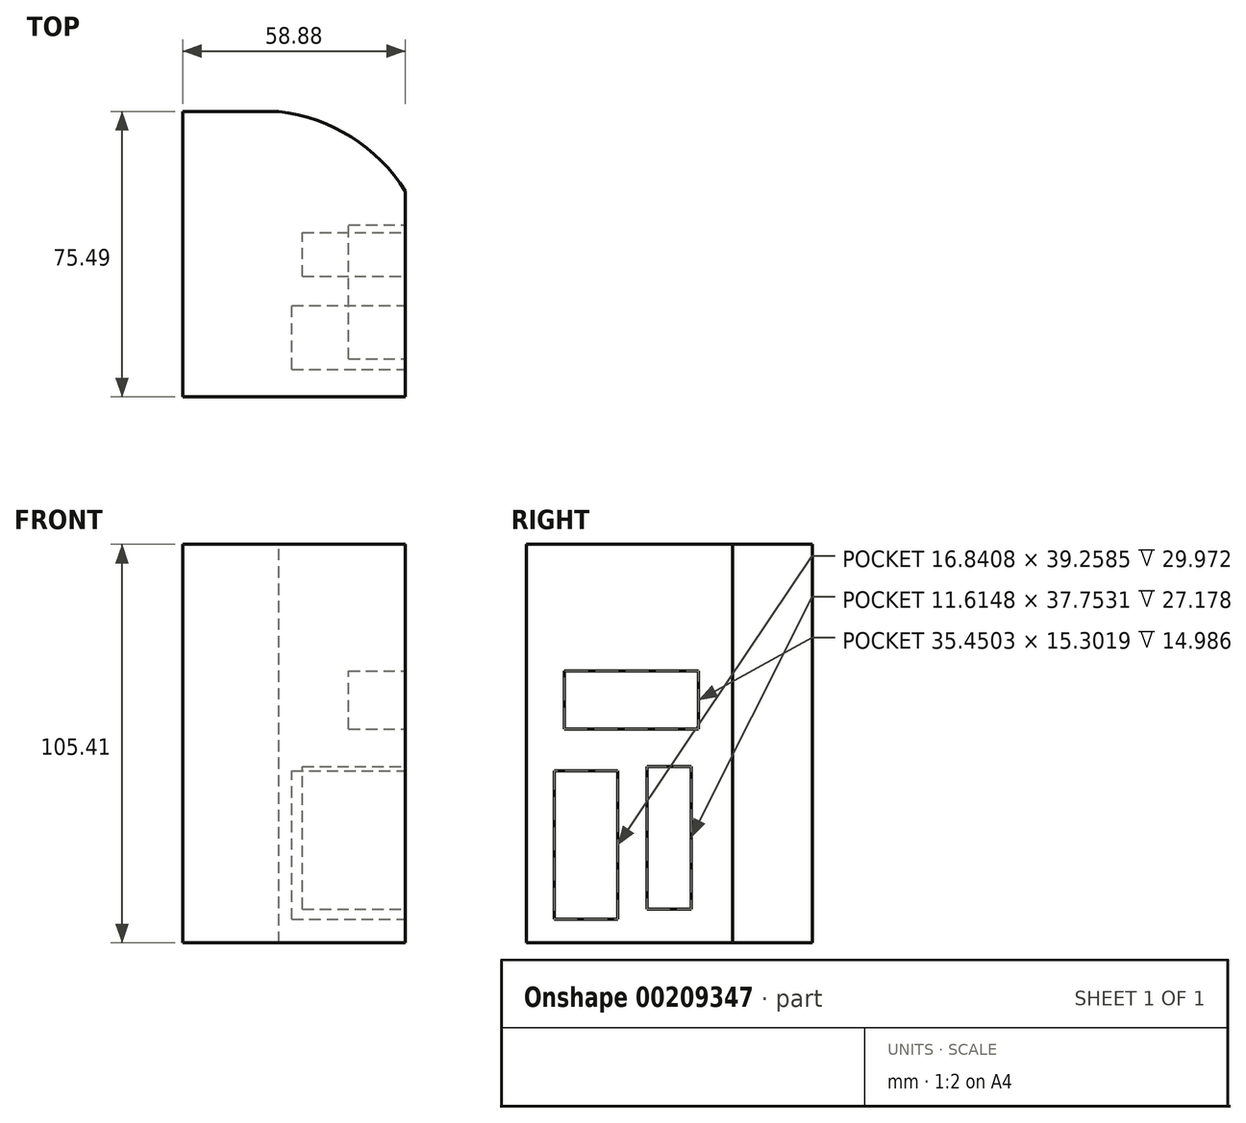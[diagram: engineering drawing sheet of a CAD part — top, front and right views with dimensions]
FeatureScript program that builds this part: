
annotation { "Feature Type Name" : "Feature", "Feature Type Description" : "" }
export const myFeature = defineFeature(function(context is Context, id is Id, definition is map)
    precondition{}
    {
        {
            var Q0;
            Q0=qCreatedBy(makeId("Top.planeOp"),FACE);
            var sketch = newSketch(context, id + "F0", { "sketchPlane" : qUnion([Q0])});
            skLineSegment(sketch, "E0.bottom", {"start": v(-30.9, 34.54) * mm, "end": v(27.98, 34.54) * mm});
            skLineSegment(sketch, "E0.top", {"start": v(-30.9, -40.95) * mm, "end": v(27.98, -40.95) * mm});
            skLineSegment(sketch, "E0.left", {"start": v(-30.9, 34.54) * mm, "end": v(-30.9, -40.95) * mm});
            skLineSegment(sketch, "E0.right", {"start": v(27.98, 34.54) * mm, "end": v(27.98, -40.95) * mm});
            skSolve(sketch);
        }
        {
            var Q0;
            Q0=makeQuery(id+"F0.imprint","IMPRINT",FACE,{"disambiguationData":[TD([[makeQuery(id+"F0.imprint","IMPRINT",EDGE,{"derivedFrom":sQuery(id+"F0.wireOp",EDGE,"E0.bottom")}),-1.0]])]});
            extrude(context, id + "F1", {"entities" : qUnion([Q0]), "depth" : 25.4 * mm});
        }
        {
            var Q0;
            Q0=makeQuery(id+"F1.opExtrude","CAP_FACE",FACE,{"disambiguationData":[OSD([sQuery(id+"F0.wireOp",EDGE,"E0.bottom"),sQuery(id+"F0.wireOp",EDGE,"E0.top"),sQuery(id+"F0.wireOp",EDGE,"E0.left"),sQuery(id+"F0.wireOp",EDGE,"E0.right")])],"isStart":false});
            var sketch = newSketch(context, id + "F2", { "sketchPlane" : qUnion([Q0])});
            skArc(sketch, "E1", {"start": v(27.98, 13.44) * mm, "mid": v(9.03, 30.36) * mm, "end": v(-16.02, 34.54) * mm});
            skSolve(sketch);
        }
        {
            var Q0;
            {var subQ0=sQuery(id+"F2.wireOp",EDGE,"E1");var subQ1=makeQuery(id+"F1.opExtrude","CAP_EDGE",EDGE,{"disambiguationData":[OSD([sQuery(id+"F0.wireOp",EDGE,"E0.right")])],"isStart":false});var subQ2=makeQuery(id+"F2.imprint","INTERSECT",VERTEX,{"derivedFrom":[subQ1,subQ0]});Q0=makeQuery(id+"F2.imprint","IMPRINT",FACE,{"disambiguationData":[TD([[makeQuery(id+"F2.imprint","IMPRINT",EDGE,{"disambiguationData":[TD([[subQ2,-1.0]])],"derivedFrom":subQ0}),-1.0]])]});}
            extrude(context, id + "F3", {"entities" : qUnion([Q0]), "operationType" : NewBodyOperationType.REMOVE, "oppositeDirection" : true, "depth" : 25.4 * mm});
        }
        {
            var Q0;
            Q0=makeQuery(id+"F1.opExtrude","CAP_FACE",FACE,{"disambiguationData":[OSD([sQuery(id+"F0.wireOp",EDGE,"E0.bottom"),sQuery(id+"F0.wireOp",EDGE,"E0.top"),sQuery(id+"F0.wireOp",EDGE,"E0.left"),sQuery(id+"F0.wireOp",EDGE,"E0.right")])],"isStart":false});
            extrude(context, id + "F4", {"entities" : qUnion([Q0]), "operationType" : NewBodyOperationType.ADD, "depth" : 80 * mm});
        }
        {
            var Q0;
            {var subQ0=sQuery(id+"F0.wireOp",EDGE,"E0.right");Q0=makeQuery(id+"F4.boolean.opBoolean","MERGE",FACE,{"derivedFrom":[makeQuery(id+"F1.opExtrude","SWEPT_FACE",FACE,{"disambiguationData":[OSD([subQ0])]}),makeQuery(id+"F4.opExtrude","SWEPT_FACE",FACE,{"disambiguationData":[OSD([subQ0])]})]});}
            var sketch = newSketch(context, id + "F5", { "sketchPlane" : qUnion([Q0])});
            skLineSegment(sketch, "E2.bottom", {"start": v(-33.67, 6.24) * mm, "end": v(-16.83, 6.24) * mm});
            skLineSegment(sketch, "E2.top", {"start": v(-33.67, 45.5) * mm, "end": v(-16.83, 45.5) * mm});
            skLineSegment(sketch, "E2.left", {"start": v(-33.67, 6.24) * mm, "end": v(-33.67, 45.5) * mm});
            skLineSegment(sketch, "E2.right", {"start": v(-16.83, 6.24) * mm, "end": v(-16.83, 45.5) * mm});
            skSolve(sketch);
        }
        {
            var Q0;
            Q0=makeQuery(id+"F5.imprint","IMPRINT",FACE,{"disambiguationData":[TD([[makeQuery(id+"F5.imprint","IMPRINT",EDGE,{"derivedFrom":sQuery(id+"F5.wireOp",EDGE,"E2.bottom")}),1.0]])]});
            extrude(context, id + "F6", {"entities" : qUnion([Q0]), "operationType" : NewBodyOperationType.REMOVE, "oppositeDirection" : true, "depth" : 29.97 * mm});
        }
        {
            var Q0;
            {var subQ0=sQuery(id+"F0.wireOp",EDGE,"E0.right");Q0=makeQuery(id+"F4.boolean.opBoolean","MERGE",FACE,{"derivedFrom":[makeQuery(id+"F1.opExtrude","SWEPT_FACE",FACE,{"disambiguationData":[OSD([subQ0])]}),makeQuery(id+"F4.opExtrude","SWEPT_FACE",FACE,{"disambiguationData":[OSD([subQ0])]})]});}
            var sketch = newSketch(context, id + "F7", { "sketchPlane" : qUnion([Q0])});
            skLineSegment(sketch, "E3.bottom", {"start": v(-9.1, 8.94) * mm, "end": v(2.52, 8.94) * mm});
            skLineSegment(sketch, "E3.top", {"start": v(-9.1, 46.7) * mm, "end": v(2.52, 46.7) * mm});
            skLineSegment(sketch, "E3.left", {"start": v(-9.1, 8.94) * mm, "end": v(-9.1, 46.7) * mm});
            skLineSegment(sketch, "E3.right", {"start": v(2.52, 8.94) * mm, "end": v(2.52, 46.7) * mm});
            skSolve(sketch);
        }
        {
            var Q0;
            Q0=makeQuery(id+"F7.imprint","IMPRINT",FACE,{"disambiguationData":[TD([[makeQuery(id+"F7.imprint","IMPRINT",EDGE,{"derivedFrom":sQuery(id+"F7.wireOp",EDGE,"E3.bottom")}),1.0]])]});
            extrude(context, id + "F8", {"entities" : qUnion([Q0]), "operationType" : NewBodyOperationType.REMOVE, "oppositeDirection" : true, "depth" : 27.18 * mm});
        }
        {
            var Q0;
            {var subQ0=sQuery(id+"F0.wireOp",EDGE,"E0.right");Q0=makeQuery(id+"F4.boolean.opBoolean","MERGE",FACE,{"derivedFrom":[makeQuery(id+"F1.opExtrude","SWEPT_FACE",FACE,{"disambiguationData":[OSD([subQ0])]}),makeQuery(id+"F4.opExtrude","SWEPT_FACE",FACE,{"disambiguationData":[OSD([subQ0])]})]});}
            var sketch = newSketch(context, id + "F9", { "sketchPlane" : qUnion([Q0])});
            skSolve(sketch);
        }
        {
            var Q0;
            {var subQ0=sQuery(id+"F0.wireOp",EDGE,"E0.right");Q0=makeQuery(id+"F9.imprint","IMPRINT",FACE,{"disambiguationData":[TD([[makeQuery(id+"F9.imprint","IMPRINT",EDGE,{"derivedFrom":makeQuery(id+"F1.opExtrude","CAP_EDGE",EDGE,{"disambiguationData":[OSD([subQ0])],"isStart":true})}),-1.0]])]});}
            var sketch = newSketch(context, id + "F10", { "sketchPlane" : qUnion([Q0])});
            skLineSegment(sketch, "E4.bottom", {"start": v(-30.92, 56.56) * mm, "end": v(4.53, 56.56) * mm});
            skLineSegment(sketch, "E4.top", {"start": v(-30.92, 71.86) * mm, "end": v(4.53, 71.86) * mm});
            skLineSegment(sketch, "E4.left", {"start": v(-30.92, 56.56) * mm, "end": v(-30.92, 71.86) * mm});
            skLineSegment(sketch, "E4.right", {"start": v(4.53, 56.56) * mm, "end": v(4.53, 71.86) * mm});
            skSolve(sketch);
        }
        {
            var Q0;
            Q0=makeQuery(id+"F10.imprint","IMPRINT",FACE,{"disambiguationData":[TD([[makeQuery(id+"F10.imprint","IMPRINT",EDGE,{"derivedFrom":sQuery(id+"F10.wireOp",EDGE,"E4.bottom")}),1.0]])]});
            extrude(context, id + "F11", {"entities" : qUnion([Q0]), "operationType" : NewBodyOperationType.REMOVE, "oppositeDirection" : true, "depth" : 15 * mm});
        }
    });
